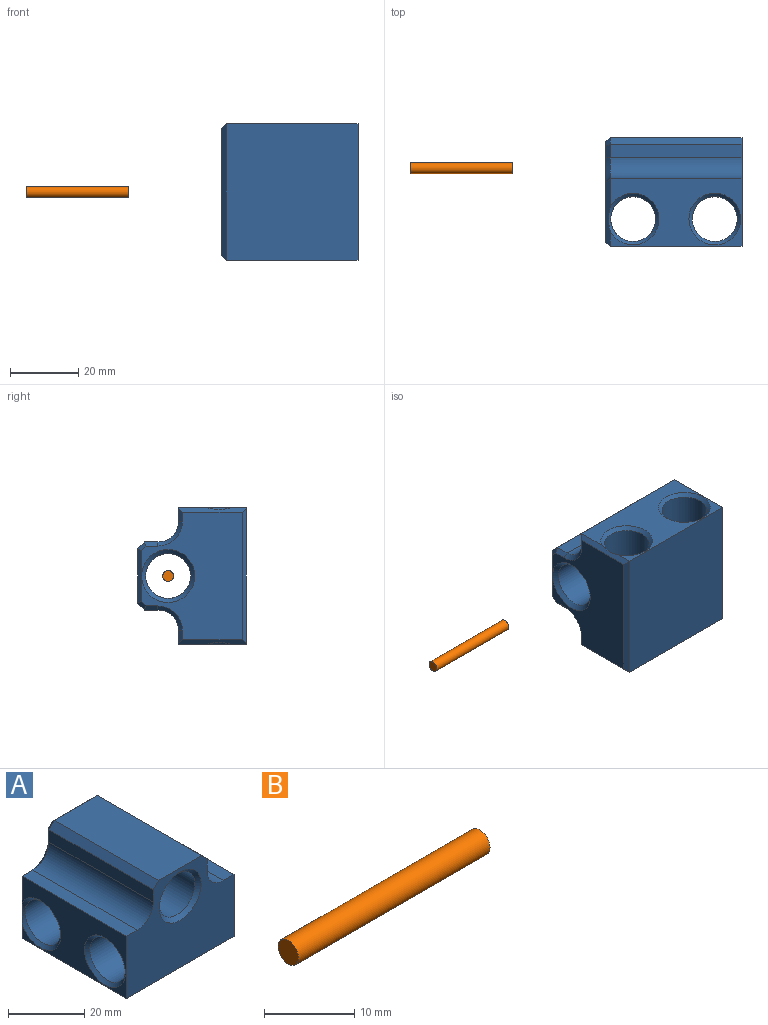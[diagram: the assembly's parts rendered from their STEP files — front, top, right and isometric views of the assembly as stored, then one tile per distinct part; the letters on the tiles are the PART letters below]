
ASSEMBLY  parts=2 mates=1
PART A: 35 faces, bbox 40x40x32 mm
  f0: plane 38.8x4mm, normal (0,0,1), area 155.2mm2, adj f4,f6,f13,f25
  f1: plane 40x38.8mm, normal (0,0,-1), area 1552mm2, adj f4,f5,f6,f21
  f2: plane 37.6x29.6mm, normal (0,1,0), area 702.4mm2, adj f17,f18,f19,f20,f21,f22,f23,f24
  f3: plane 38.8x4mm, normal (0,0,1), area 155.2mm2, adj f4,f5,f14,f17
  f4: plane 40x32mm, normal (0,-1,0), area 860.3mm2, adj f0,f1,f3,f5,f6,f9,f10,f11
  f5: plane 38.8x20mm, normal (1,0,0), area 416.7mm2, adj f1,f3,f4,f19,f32,f34
  f6: plane 38.8x20mm, normal (-1,0,0), area 416.7mm2, adj f0,f1,f4,f23,f31,f33
  f7: cylinder r=6.6mm len=38mm, axis (1,0,0), area 1575.8mm2, adj f33,f34
  f8: cylinder r=6.6mm len=38mm, axis (1,0,0), area 1575.8mm2, adj f31,f32
  f9: plane 38.8x4mm, normal (-1,0,0), area 155.2mm2, adj f4,f13,f16,f28
  f10: plane 38.8x4mm, normal (1,0,0), area 155.2mm2, adj f4,f14,f15,f20
  f11: plane 38.8x16mm, normal (0,0,1), area 620.8mm2, adj f4,f15,f16,f24
  f12: cylinder r=6.6mm len=37.6mm, axis (0,-1,0), area 1559.2mm2, adj f29,f30
  f13: cylinder r=6mm len=38.8mm, axis (0,1,0), area 365.7mm2, adj f0,f4,f9,f27
  f14: cylinder r=6mm len=38.8mm, axis (0,-1,0), area 365.7mm2, adj f3,f4,f10,f18
  f15: plane 38.8x2mm, normal (0.71,0,0.71), area 109.7mm2, adj f4,f10,f11,f22
  f16: plane 38.8x2mm, normal (-0.71,0,0.71), area 109.7mm2, adj f4,f9,f11,f26
  f17: plane 4x1.2mm, normal (0,0.71,0.71), area 5.8mm2, adj f2,f3,f18,f19
  f18: cone r=7.2mm half-angle=45deg, axis (0,1,0), area 17.6mm2, adj f2,f14,f17,f20
  f19: plane 20x1.2mm, normal (0.71,0.71,0), area 29.3mm2, adj f2,f5,f17,f21,f34
  f20: plane 4x1.2mm, normal (0.71,0.71,0), area 6.4mm2, adj f2,f10,f18,f22
  f21: plane 40x1.2mm, normal (0,0.71,-0.71), area 65.8mm2, adj f1,f2,f19,f23
  f22: plane 2.5x2.5mm, normal (0.5,0.71,0.5), area 4mm2, adj f2,f15,f20,f24
  f23: plane 20x1.2mm, normal (-0.71,0.71,0), area 29.3mm2, adj f2,f6,f21,f25,f33
  f24: plane 16x1.2mm, normal (0,0.71,0.71), area 26.3mm2, adj f2,f11,f22,f26
  f25: plane 4x1.2mm, normal (0,0.71,0.71), area 5.8mm2, adj f0,f2,f23,f27
  f26: plane 2.5x2.5mm, normal (-0.5,0.71,0.5), area 4mm2, adj f2,f16,f24,f28
  f27: cone r=7.2mm half-angle=45deg, axis (0,1,0), area 17.6mm2, adj f2,f13,f25,f28
  f28: plane 4x1.2mm, normal (-0.71,0.71,0), area 6.4mm2, adj f2,f9,f26,f27
  f29: cone r=6.6mm half-angle=45deg, axis (0,-1,0), area 76.8mm2, adj f4,f12
  f30: cone r=7.8mm half-angle=45deg, axis (0,1,0), area 76.8mm2, adj f2,f12
  f31: cone r=7.6mm half-angle=45deg, axis (-1,0,0), area 63.1mm2, adj f6,f8
  f32: cone r=6.6mm half-angle=45deg, axis (1,0,0), area 63.1mm2, adj f5,f8
  f33: cone r=7.6mm half-angle=45deg, axis (-1,0,0), area 60.5mm2, adj f6,f7,f23
  f34: cone r=6.6mm half-angle=45deg, axis (1,0,0), area 60.5mm2, adj f5,f7,f19
PART B: 3 faces, bbox 30x3.2x3.2 mm
  f0: cylinder r=1.6mm len=30mm, axis (1,0,0), area 301.6mm2, adj f1,f2
  f1: plane 3.2x3.2mm, normal (-1,0,0), area 8mm2, adj f0
  f2: plane 3.2x3.2mm, normal (1,0,0), area 8mm2, adj f0
PLACE A rot(axis=(-0.58,0.58,0.58),120deg) t=(21.49,13.51,9.16)mm fixed
PLACE B rot(axis=(1,0,0),25.2deg) t=(-41.14,26.51,9.16)mm
MATE cylindrical A.f12 <-> B.f0  axis (1,0,0) through (2.69,26.51,9.16)mm
